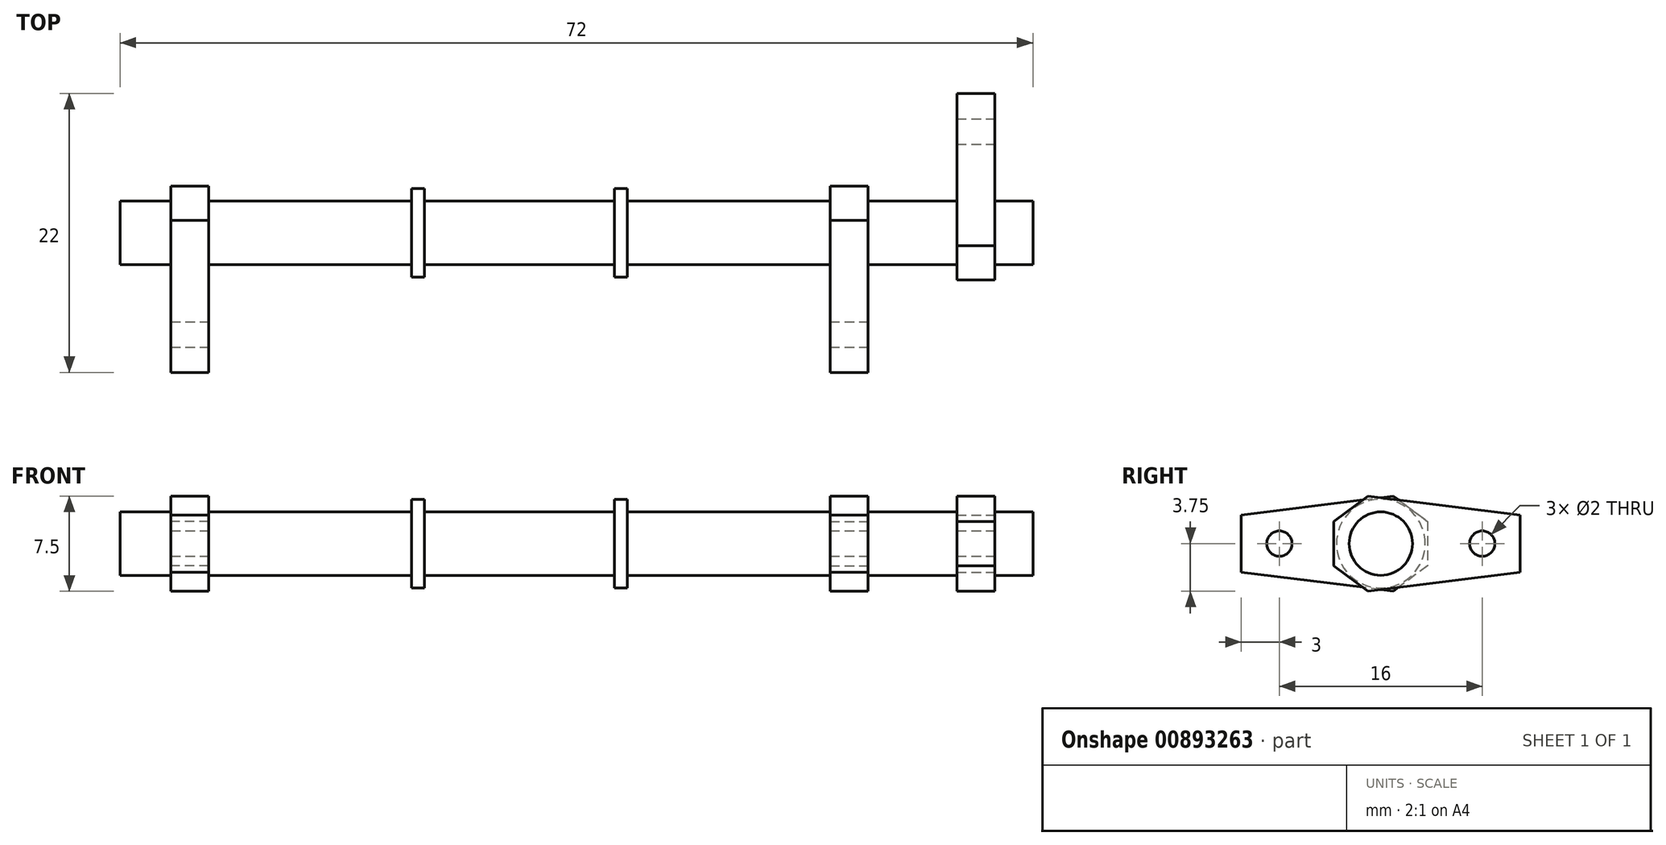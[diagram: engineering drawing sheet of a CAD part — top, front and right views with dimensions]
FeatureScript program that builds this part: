
annotation { "Feature Type Name" : "Feature", "Feature Type Description" : "" }
export const myFeature = defineFeature(function(context is Context, id is Id, definition is map)
    precondition{}
    {
        {
            var Q0;
            Q0=qCreatedBy(makeId("Right.planeOp"),FACE);
            var sketch = newSketch(context, id + "F0", { "sketchPlane" : qUnion([Q0])});
            skCircle(sketch, "E0", {"center": v(0, 0) * mm, "radius": 2.5 * mm});
            skSolve(sketch);
        }
        {
            var Q0;
            Q0 = qSketchRegion(id + "F0", true);
            extrude(context, id + "F1", {"entities" : qUnion([Q0]), "endBound" : BoundingType.SYMMETRIC, "depth" : 72 * mm, "offsetDistance" : 25 * mm});
        }
        {
            var Q0;
            Q0=qCreatedBy(makeId("Right.planeOp"),FACE);
            cPlane(context, id + "F2", {"entities" : qUnion([Q0]), "cplaneType" : CPlaneType.OFFSET, "offset" : 32 * mm, "oppositeDirection" : true, "width" : 150 * mm, "height" : 150 * mm});
        }
        {
            var Q0;
            Q0=qCreatedBy(id+"F2.planeOp",FACE);
            var sketch = newSketch(context, id + "F3", { "sketchPlane" : qUnion([Q0])});
            skLineSegment(sketch, "E1", {"start": v(3.7, 1.75) * mm, "end": v(3.7, -1.75) * mm});
            skLineSegment(sketch, "E2", {"start": v(3.7, -1.75) * mm, "end": v(1, -3.75) * mm});
            skLineSegment(sketch, "E3", {"start": v(1, -3.75) * mm, "end": v(-11, -2.25) * mm});
            skLineSegment(sketch, "E4", {"start": v(-11, -2.25) * mm, "end": v(-11, 2.25) * mm});
            skLineSegment(sketch, "E5", {"start": v(-11, 2.25) * mm, "end": v(1, 3.75) * mm});
            skLineSegment(sketch, "E6", {"start": v(1, 3.75) * mm, "end": v(3.7, 1.75) * mm});
            skSolve(sketch);
        }
        {
            var Q0;
            Q0 = qSketchRegion(id + "F3", true);
            extrude(context, id + "F4", {"entities" : qUnion([Q0]), "operationType" : NewBodyOperationType.ADD, "depth" : 3 * mm, "offsetDistance" : 25 * mm});
        }
        {
            var Q0;
            Q0=qCreatedBy(makeId("Right.planeOp"),FACE);
            cPlane(context, id + "F5", {"entities" : qUnion([Q0]), "cplaneType" : CPlaneType.OFFSET, "offset" : 13 * mm, "oppositeDirection" : true, "width" : 150 * mm, "height" : 150 * mm});
        }
        {
            var Q0;
            Q0=qCreatedBy(id+"F5.planeOp",FACE);
            var sketch = newSketch(context, id + "F6", { "sketchPlane" : qUnion([Q0])});
            skCircle(sketch, "E7", {"center": v(0, 0) * mm, "radius": 3.5 * mm});
            skSolve(sketch);
        }
        {
            var Q0;
            Q0 = qSketchRegion(id + "F6", true);
            extrude(context, id + "F7", {"entities" : qUnion([Q0]), "operationType" : NewBodyOperationType.ADD, "depth" : 1 * mm, "offsetDistance" : 25 * mm});
        }
        {
            var Q0;
            Q0=qCreatedBy(id+"F5.planeOp",FACE);
            cPlane(context, id + "F8", {"entities" : qUnion([Q0]), "cplaneType" : CPlaneType.OFFSET, "offset" : 16 * mm, "width" : 150 * mm, "height" : 150 * mm});
        }
        {
            var Q0;
            Q0=qCreatedBy(id+"F8.planeOp",FACE);
            var sketch = newSketch(context, id + "F9", { "sketchPlane" : qUnion([Q0])});
            skCircle(sketch, "E8", {"center": v(0, 0) * mm, "radius": 3.5 * mm});
            skSolve(sketch);
        }
        {
            var Q0;
            Q0 = qSketchRegion(id + "F9", true);
            extrude(context, id + "F10", {"entities" : qUnion([Q0]), "operationType" : NewBodyOperationType.ADD, "depth" : 1 * mm, "offsetDistance" : 25 * mm});
        }
        {
            var Q0;
            Q0=qCreatedBy(makeId("Right.planeOp"),FACE);
            cPlane(context, id + "F11", {"entities" : qUnion([Q0]), "cplaneType" : CPlaneType.OFFSET, "offset" : 33 * mm, "width" : 150 * mm, "height" : 150 * mm});
        }
        {
            var Q0;
            Q0=qCreatedBy(id+"F11.planeOp",FACE);
            var sketch = newSketch(context, id + "F12", { "sketchPlane" : qUnion([Q0])});
            skLineSegment(sketch, "E9", {"start": v(-3.7, 1.75) * mm, "end": v(-3.7, -1.75) * mm});
            skLineSegment(sketch, "E10", {"start": v(-3.7, -1.75) * mm, "end": v(-1, -3.75) * mm});
            skLineSegment(sketch, "E11", {"start": v(-1, -3.75) * mm, "end": v(11, -2.25) * mm});
            skLineSegment(sketch, "E12", {"start": v(11, -2.25) * mm, "end": v(11, 2.25) * mm});
            skLineSegment(sketch, "E13", {"start": v(11, 2.25) * mm, "end": v(-1, 3.75) * mm});
            skLineSegment(sketch, "E14", {"start": v(-1, 3.75) * mm, "end": v(-3.7, 1.75) * mm});
            skSolve(sketch);
        }
        {
            var Q0;
            Q0 = qSketchRegion(id + "F12", true);
            extrude(context, id + "F13", {"entities" : qUnion([Q0]), "operationType" : NewBodyOperationType.ADD, "oppositeDirection" : true, "depth" : 3 * mm, "offsetDistance" : 25 * mm});
        }
        {
            var Q0;
            Q0=qCreatedBy(makeId("Right.planeOp"),FACE);
            cPlane(context, id + "F14", {"entities" : qUnion([Q0]), "cplaneType" : CPlaneType.OFFSET, "offset" : 23 * mm, "width" : 150 * mm, "height" : 150 * mm});
        }
        {
            var Q0;
            Q0=qCreatedBy(id+"F14.planeOp",FACE);
            var sketch = newSketch(context, id + "F15", { "sketchPlane" : qUnion([Q0])});
            skLineSegment(sketch, "E15", {"start": v(3.7, 1.75) * mm, "end": v(3.7, -1.75) * mm});
            skLineSegment(sketch, "E16", {"start": v(3.7, -1.75) * mm, "end": v(1, -3.75) * mm});
            skLineSegment(sketch, "E17", {"start": v(1, -3.75) * mm, "end": v(-11, -2.25) * mm});
            skLineSegment(sketch, "E18", {"start": v(-11, -2.25) * mm, "end": v(-11, 2.25) * mm});
            skLineSegment(sketch, "E19", {"start": v(-11, 2.25) * mm, "end": v(1, 3.75) * mm});
            skLineSegment(sketch, "E20", {"start": v(1, 3.75) * mm, "end": v(3.7, 1.75) * mm});
            skSolve(sketch);
        }
        {
            var Q0;
            Q0 = qSketchRegion(id + "F15", true);
            extrude(context, id + "F16", {"entities" : qUnion([Q0]), "operationType" : NewBodyOperationType.ADD, "oppositeDirection" : true, "depth" : 3 * mm, "offsetDistance" : 25 * mm});
        }
        {
            var Q0;
            Q0=makeQuery(id+"F16.opExtrude","CAP_FACE",FACE,{"disambiguationData":[OSD([sQuery(id+"F15.wireOp",EDGE,"E15"),sQuery(id+"F15.wireOp",EDGE,"E16"),sQuery(id+"F15.wireOp",EDGE,"E17"),sQuery(id+"F15.wireOp",EDGE,"E18"),sQuery(id+"F15.wireOp",EDGE,"E19"),sQuery(id+"F15.wireOp",EDGE,"E20")])],"isStart":true});
            var sketch = newSketch(context, id + "F17", { "sketchPlane" : qUnion([Q0])});
            skCircle(sketch, "E21", {"center": v(-8, 0) * mm, "radius": 1 * mm});
            skSolve(sketch);
        }
        {
            var Q0;
            Q0=makeQuery(id+"F13.opExtrude","CAP_FACE",FACE,{"disambiguationData":[OSD([sQuery(id+"F12.wireOp",EDGE,"E9"),sQuery(id+"F12.wireOp",EDGE,"E10"),sQuery(id+"F12.wireOp",EDGE,"E11"),sQuery(id+"F12.wireOp",EDGE,"E12"),sQuery(id+"F12.wireOp",EDGE,"E13"),sQuery(id+"F12.wireOp",EDGE,"E14")])],"isStart":true});
            var sketch = newSketch(context, id + "F18", { "sketchPlane" : qUnion([Q0])});
            skCircle(sketch, "E22", {"center": v(8, 0) * mm, "radius": 1 * mm});
            skSolve(sketch);
        }
        {
            var Q0;
            Q0 = qSketchRegion(id + "F18", true);
            extrude(context, id + "F19", {"entities" : qUnion([Q0]), "operationType" : NewBodyOperationType.REMOVE, "endBound" : BoundingType.THROUGH_ALL, "oppositeDirection" : true, "depth" : 25 * mm, "offsetDistance" : 25 * mm});
        }
        {
            var Q0;
            Q0 = qSketchRegion(id + "F17", true);
            extrude(context, id + "F20", {"entities" : qUnion([Q0]), "operationType" : NewBodyOperationType.REMOVE, "endBound" : BoundingType.THROUGH_ALL, "oppositeDirection" : true, "depth" : 25 * mm, "offsetDistance" : 25 * mm});
        }
    });
